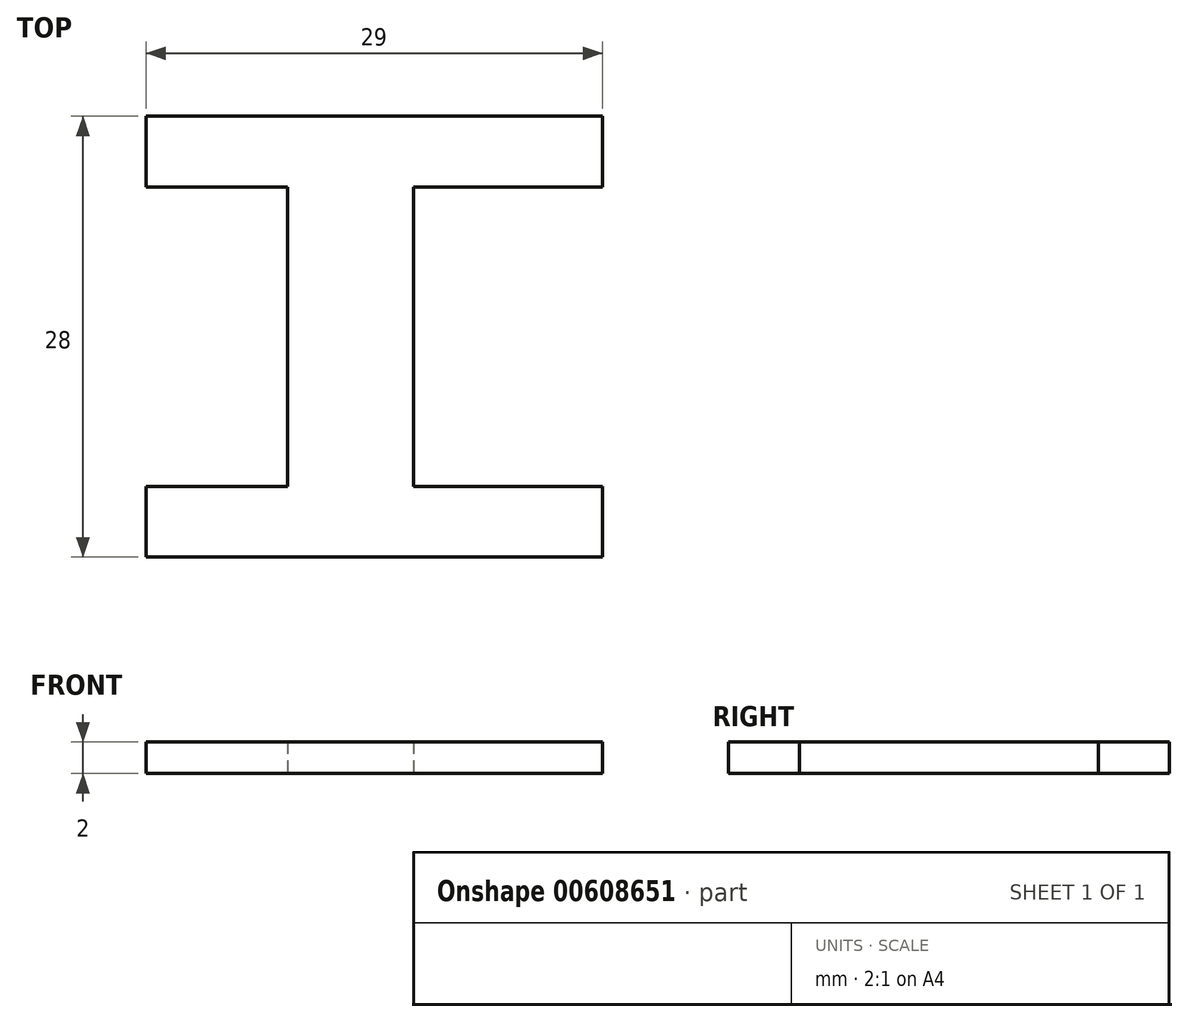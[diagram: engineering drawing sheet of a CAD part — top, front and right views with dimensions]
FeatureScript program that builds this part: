
annotation { "Feature Type Name" : "Feature", "Feature Type Description" : "" }
export const myFeature = defineFeature(function(context is Context, id is Id, definition is map)
    precondition{}
    {
        {
            var Q0;
            Q0=qCreatedBy(makeId("Top.planeOp"),FACE);
            var sketch = newSketch(context, id + "F0", { "sketchPlane" : qUnion([Q0])});
            skLineSegment(sketch, "E0.bottom", {"start": v(-13.12, -9.67) * mm, "end": v(15.88, -9.67) * mm});
            skLineSegment(sketch, "E0.top", {"start": v(-13.12, -14.17) * mm, "end": v(15.88, -14.17) * mm});
            skLineSegment(sketch, "E0.left", {"start": v(-13.12, -9.67) * mm, "end": v(-13.12, -14.17) * mm});
            skLineSegment(sketch, "E0.right", {"start": v(15.88, -9.67) * mm, "end": v(15.88, -14.17) * mm});
            skLineSegment(sketch, "E1.bottom", {"start": v(-13.12, 13.83) * mm, "end": v(15.88, 13.83) * mm});
            skLineSegment(sketch, "E1.top", {"start": v(-13.12, 9.33) * mm, "end": v(15.88, 9.33) * mm});
            skLineSegment(sketch, "E1.left", {"start": v(-13.12, 13.83) * mm, "end": v(-13.12, 9.33) * mm});
            skLineSegment(sketch, "E1.right", {"start": v(15.88, 13.83) * mm, "end": v(15.88, 9.33) * mm});
            skLineSegment(sketch, "E2.bottom", {"start": v(3.88, 9.33) * mm, "end": v(-4.12, 9.33) * mm});
            skLineSegment(sketch, "E2.top", {"start": v(3.88, -9.67) * mm, "end": v(-4.12, -9.67) * mm});
            skLineSegment(sketch, "E2.left", {"start": v(3.88, 9.33) * mm, "end": v(3.88, -9.67) * mm});
            skLineSegment(sketch, "E2.right", {"start": v(-4.12, 9.33) * mm, "end": v(-4.12, -9.67) * mm});
            skSolve(sketch);
        }
        {
            var Q0;
            Q0 = qSketchRegion(id + "F0", true);
            extrude(context, id + "F1", {"entities" : qUnion([Q0]), "depth" : 2 * mm, "offsetDistance" : 25 * mm});
        }
    });
